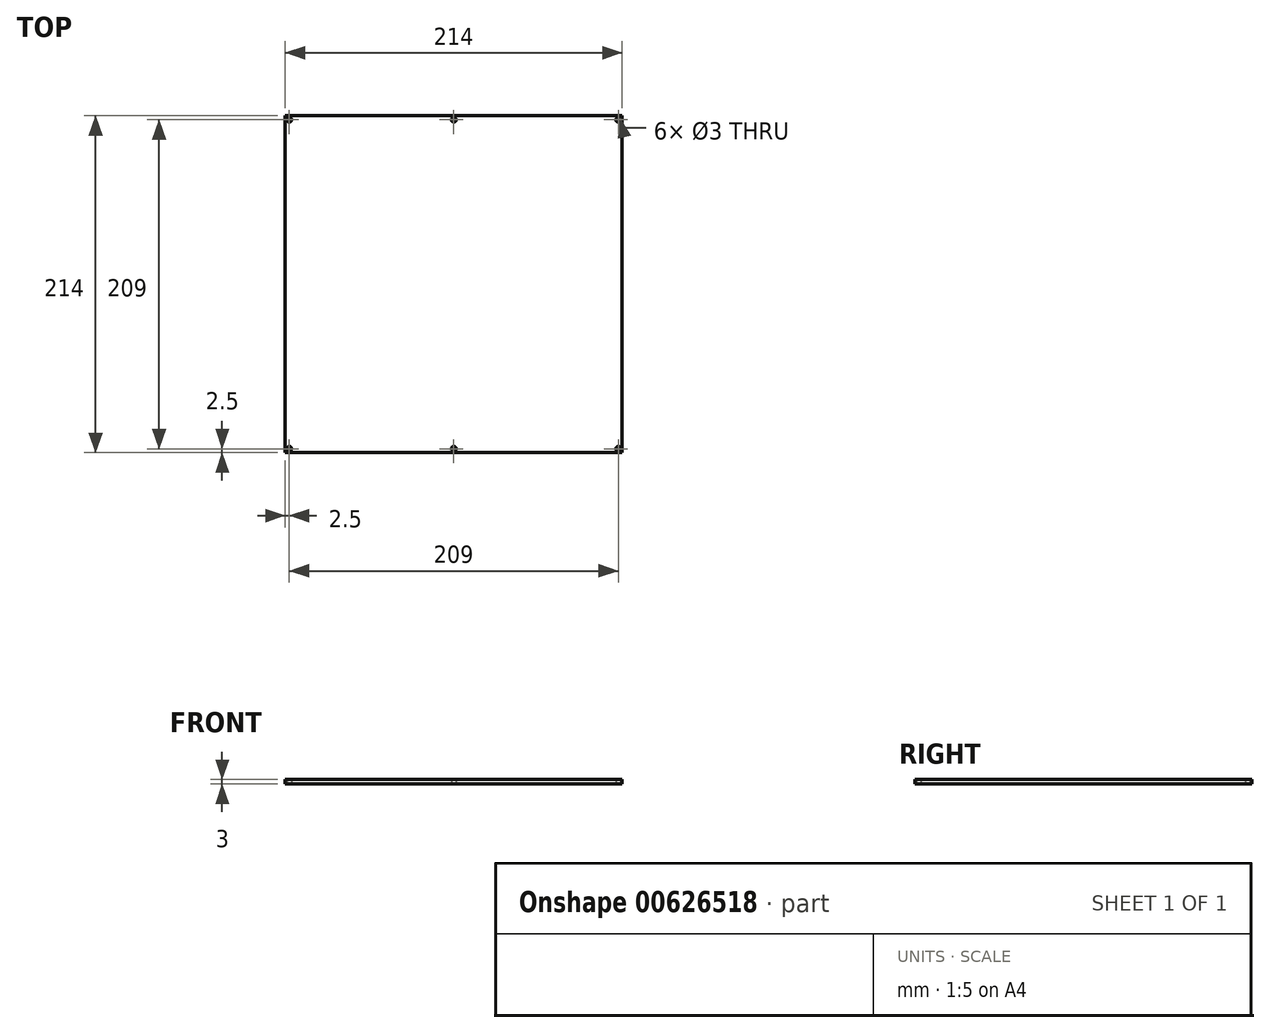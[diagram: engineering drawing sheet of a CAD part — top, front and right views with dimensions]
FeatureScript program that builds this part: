
annotation { "Feature Type Name" : "Feature", "Feature Type Description" : "" }
export const myFeature = defineFeature(function(context is Context, id is Id, definition is map)
    precondition{}
    {
        {
            var Q0;
            Q0=qCreatedBy(makeId("Top.planeOp"),FACE);
            var sketch = newSketch(context, id + "F0", { "sketchPlane" : qUnion([Q0]), "asVersion" : FeatureScriptVersionNumber.V275_SKETCH_PATTERN_LOWER_LIMIT});
            skLineSegment(sketch, "E0", {"start": v(0, 0) * mm, "end": v(-107, 107) * mm, "construction": true});
            skCircle(sketch, "E1", {"center": v(-104.5, 104.5) * mm, "radius": 1.5 * mm});
            skLineSegment(sketch, "E2.MirrorCS", {"start": v(0, 0) * mm, "end": v(107, 107) * mm, "construction": true});
            skCircle(sketch, "E3.MirrorC", {"center": v(104.5, 104.5) * mm, "radius": 1.5 * mm});
            skCircle(sketch, "E4.MirrorC", {"center": v(-104.5, -104.5) * mm, "radius": 1.5 * mm});
            skLineSegment(sketch, "E5.MirrorCS", {"start": v(0, 0) * mm, "end": v(-107, -107) * mm, "construction": true});
            skCircle(sketch, "E6.MirrorC", {"center": v(104.5, -104.5) * mm, "radius": 1.5 * mm});
            skLineSegment(sketch, "E7.MirrorCS", {"start": v(0, 0) * mm, "end": v(107, -107) * mm, "construction": true});
            skLineSegment(sketch, "E8", {"start": v(-107, -107) * mm, "end": v(107, -107) * mm});
            skLineSegment(sketch, "E9", {"start": v(107, -107) * mm, "end": v(107, 107) * mm});
            skLineSegment(sketch, "E10", {"start": v(107, 107) * mm, "end": v(-107, 107) * mm});
            skLineSegment(sketch, "E11", {"start": v(-107, 107) * mm, "end": v(-107, -107) * mm});
            skCircle(sketch, "E12", {"center": v(0, -104.5) * mm, "radius": 1.5 * mm});
            skCircle(sketch, "E13.MirrorC", {"center": v(0, 104.5) * mm, "radius": 1.5 * mm});
            skSolve(sketch);
        }
        {
            var Q0;
            Q0=qSketchRegion(id+"F0",true);
            extrude(context, id + "F1", {"entities" : qUnion([Q0]), "depth" : 3 * mm});
        }
    });
